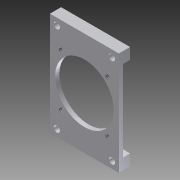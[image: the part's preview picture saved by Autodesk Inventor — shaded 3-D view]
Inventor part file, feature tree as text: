
AUTODESK INVENTOR PART (.ipt)
format: ipt  version: 2012 (Build 160160000, 160)  size: 134,656 bytes
history: native  units: in
note: dims shown in document units (in); Inventor stores cm internally (conversion verified against a paired STEP export)
features: sketch x2, extrude x2, hole x1
ambient origin geometry x8: Origin, YZ Plane, XZ Plane, XY Plane, X Axis, Y Axis, Z Axis, Center Point
bodies: Solid1 (feature_tree)
feature tree (5):
  sketch  "Sketch1"  dims[d0=1.7in d1=3.0in]
  extrude  "Extrusion1"  Depth=3.0in
  extrude  "Extrusion2"  Depth=2.0in
  hole  "Hole1"  [1 undecoded]
  sketch  "Sketch2"  dims[d2=1.5in d3=2.0in d4=1.0in d5=0.18in d6=0.2in d7=0.2in d8=1.5in d9=0.18in d10=0.2in d11=0.2in d12=0.18in d13=0.18in d14=0.125in d15=0.0in d16=0.325in d17=0.325in d18=0.2in d19=0.0in d20=2.6in d21=1.6in d23=1.35in d24=0.75in d25=0.75in d26=0.675in d27=0.13in d28=0.75in d29=0.375in d30=0.25in d31=0.5635in d32=1.0in d33=0.8108in]
note: 1 required parameter value undecoded (feature->parameter linkage not recoverable at this tier; creation-order binding heuristic only, values carry confidence <= 0.55)
